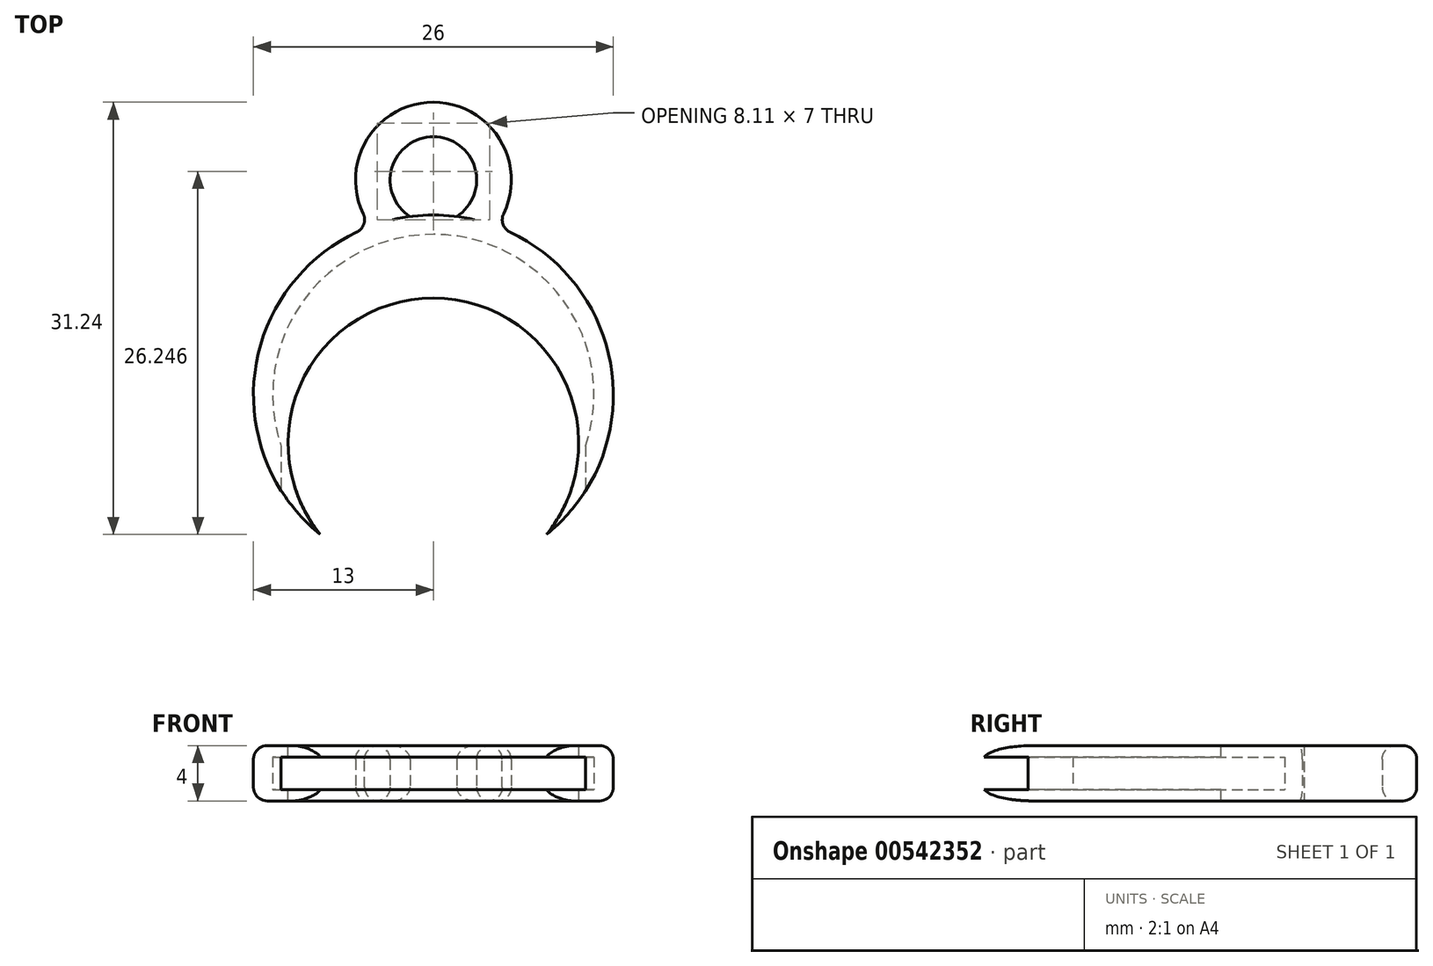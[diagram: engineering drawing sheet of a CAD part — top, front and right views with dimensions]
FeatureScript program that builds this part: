
annotation { "Feature Type Name" : "Feature", "Feature Type Description" : "" }
export const myFeature = defineFeature(function(context is Context, id is Id, definition is map)
    precondition{}
    {
        {
            var Q0;
            Q0=qCreatedBy(makeId("Top.planeOp"),FACE);
            var sketch = newSketch(context, id + "F0", { "sketchPlane" : qUnion([Q0])});
            skCircle(sketch, "E0", {"center": v(0, 0) * mm, "radius": 13 * mm});
            skArc(sketch, "E1", {"start": v(4.53, 12.19) * mm, "mid": v(0, 21.15) * mm, "end": v(-4.53, 12.19) * mm});
            skArc(sketch, "E2", {"start": v(1.68, 12.9) * mm, "mid": v(0, 18.65) * mm, "end": v(-1.68, 12.9) * mm});
            skSolve(sketch);
        }
        {
            var Q0;
            {var subQ0=sQuery(id+"F0.wireOp",EDGE,"E1");var subQ1=sQuery(id+"F0.wireOp",EDGE,"E0");var subQ2=makeQuery(id+"F0.imprint","INTERSECT",VERTEX,{"disambiguationData":[OD(0.0)],"derivedFrom":[subQ1,subQ0]});Q0=makeQuery(id+"F0.imprint","IMPRINT",FACE,{"disambiguationData":[TD([[makeQuery(id+"F0.imprint","IMPRINT",EDGE,{"disambiguationData":[TD([[subQ2,-1.0]])],"derivedFrom":subQ1}),1.0]])]});}
            var Q1;
            {var subQ0=sQuery(id+"F0.wireOp",EDGE,"E1");Q1=makeQuery(id+"F0.imprint","IMPRINT",FACE,{"disambiguationData":[TD([[makeQuery(id+"F0.imprint","IMPRINT",EDGE,{"derivedFrom":subQ0}),1.0]])]});}
            extrude(context, id + "F1", {"entities" : qUnion([Q0, Q1]), "endBound" : BoundingType.SYMMETRIC, "depth" : 4 * mm, "offsetDistance" : 25 * mm});
        }
        {
            var Q0;
            {var subQ0=sQuery(id+"F0.wireOp",EDGE,"E1");var subQ1=sQuery(id+"F0.wireOp",EDGE,"E0");Q0=makeQuery(id+"F1.opExtrude","SWEPT_EDGE",EDGE,{"disambiguationData":[OSD([subQ1,subQ0]),TDD([makeQuery(id+"F0.imprint","INTERSECT",VERTEX,{"disambiguationData":[OD(0.0)],"derivedFrom":[subQ1,subQ0]})])]});}
            fillet(context, id + "F2", {"entities" : qUnion([Q0]), "radius" : 1 * mm, "tangentPropagation" : true, "allowEdgeOverflow" : false});
        }
        {
            var Q0;
            {var subQ0=sQuery(id+"F0.wireOp",EDGE,"E1");var subQ1=sQuery(id+"F0.wireOp",EDGE,"E0");Q0=makeQuery(id+"F1.opExtrude","SWEPT_EDGE",EDGE,{"disambiguationData":[OSD([subQ1,subQ0]),TDD([makeQuery(id+"F0.imprint","INTERSECT",VERTEX,{"disambiguationData":[OD(1.0)],"derivedFrom":[subQ1,subQ0]})])]});}
            fillet(context, id + "F3", {"entities" : qUnion([Q0]), "radius" : 1 * mm, "tangentPropagation" : true, "allowEdgeOverflow" : false});
        }
        {
            var Q0;
            Q0=makeQuery(id+"F1.opExtrude","CAP_EDGE",EDGE,{"disambiguationData":[OSD([sQuery(id+"F0.wireOp",EDGE,"E2")])],"isStart":false});
            fillet(context, id + "F4", {"entities" : qUnion([Q0]), "radius" : 1 * mm, "tangentPropagation" : true, "allowEdgeOverflow" : false});
        }
        {
            var Q0;
            Q0=makeQuery(id+"F1.opExtrude","CAP_EDGE",EDGE,{"disambiguationData":[OSD([sQuery(id+"F0.wireOp",EDGE,"E2")])],"isStart":true});
            fillet(context, id + "F5", {"entities" : qUnion([Q0]), "radius" : 1 * mm, "tangentPropagation" : true, "allowEdgeOverflow" : false});
        }
        {
            var Q0;
            Q0=qCreatedBy(makeId("Top.planeOp"),FACE);
            var sketch = newSketch(context, id + "F6", { "sketchPlane" : qUnion([Q0])});
            skCircle(sketch, "E3", {"center": v(0, -3.5) * mm, "radius": 10.5 * mm});
            skSolve(sketch);
        }
        {
            var Q0;
            Q0 = qSketchRegion(id + "F6", true);
            extrude(context, id + "F7", {"entities" : qUnion([Q0]), "operationType" : NewBodyOperationType.REMOVE, "endBound" : BoundingType.SYMMETRIC, "oppositeDirection" : true, "depth" : 25 * mm, "offsetDistance" : 25 * mm});
        }
        {
            var Q0;
            Q0=qCreatedBy(makeId("Top.planeOp"),FACE);
            var sketch = newSketch(context, id + "F8", { "sketchPlane" : qUnion([Q0])});
            skCircle(sketch, "E4", {"center": v(0, 0) * mm, "radius": 11.6 * mm});
            skLineSegment(sketch, "E5.bottom", {"start": v(-11, -3.7) * mm, "end": v(11, -3.7) * mm});
            skLineSegment(sketch, "E5.top", {"start": v(-11, -18.04) * mm, "end": v(11, -18.04) * mm});
            skLineSegment(sketch, "E5.left", {"start": v(-11, -3.7) * mm, "end": v(-11, -18.04) * mm});
            skLineSegment(sketch, "E5.right", {"start": v(11, -3.7) * mm, "end": v(11, -18.04) * mm});
            skSolve(sketch);
        }
        {
            var Q0;
            Q0 = qSketchRegion(id + "F8", true);
            extrude(context, id + "F9", {"entities" : qUnion([Q0]), "operationType" : NewBodyOperationType.REMOVE, "endBound" : BoundingType.SYMMETRIC, "depth" : 2.34 * mm, "offsetDistance" : 25 * mm});
        }
        {
            var Q0;
            {var subQ0=sQuery(id+"F0.wireOp",EDGE,"E1");var subQ1=sQuery(id+"F0.wireOp",EDGE,"E0");var subQ2=makeQuery(id+"F0.imprint","IMPRINT",EDGE,{"disambiguationData":[TD([[makeQuery(id+"F0.imprint","INTERSECT",VERTEX,{"disambiguationData":[OD(0.0)],"derivedFrom":[subQ1,subQ0]}),1.0]])],"derivedFrom":subQ1});Q0=makeQuery(id+"F7.boolean.opBoolean","SPLIT",EDGE,{"disambiguationData":[TD([makeQuery(id+"F2.opFillet","BLEND_FACE",FACE,{"disambiguationData":[OSD([subQ1,subQ0])]})])],"derivedFrom":makeQuery(id+"F1.opExtrude","CAP_EDGE",EDGE,{"disambiguationData":[OSD([subQ1]),TDD([subQ2])],"isStart":false})});}
            var Q1;
            {var subQ0=sQuery(id+"F0.wireOp",EDGE,"E1");var subQ1=sQuery(id+"F0.wireOp",EDGE,"E0");var subQ2=makeQuery(id+"F0.imprint","IMPRINT",EDGE,{"disambiguationData":[TD([[makeQuery(id+"F0.imprint","INTERSECT",VERTEX,{"disambiguationData":[OD(0.0)],"derivedFrom":[subQ1,subQ0]}),1.0]])],"derivedFrom":subQ1});Q1=makeQuery(id+"F7.boolean.opBoolean","SPLIT",EDGE,{"disambiguationData":[TD([makeQuery(id+"F3.opFillet","BLEND_FACE",FACE,{"disambiguationData":[OSD([subQ1,subQ0])]})])],"derivedFrom":makeQuery(id+"F1.opExtrude","CAP_EDGE",EDGE,{"disambiguationData":[OSD([subQ1]),TDD([subQ2])],"isStart":false})});}
            var Q2;
            Q2=makeQuery(id+"F1.opExtrude","CAP_EDGE",EDGE,{"disambiguationData":[OSD([sQuery(id+"F0.wireOp",EDGE,"E1")])],"isStart":false});
            var Q3;
            Q3=makeQuery(id+"F1.opExtrude","CAP_EDGE",EDGE,{"disambiguationData":[OSD([sQuery(id+"F0.wireOp",EDGE,"E1")])],"isStart":true});
            var Q4;
            {var subQ0=sQuery(id+"F0.wireOp",EDGE,"E1");var subQ1=sQuery(id+"F0.wireOp",EDGE,"E0");Q4=makeQuery(id+"F3.opFillet","BLEND_EDGE",EDGE,{"blendedFrom":[makeQuery(id+"F1.opExtrude","SWEPT_EDGE",EDGE,{"disambiguationData":[OSD([subQ1,subQ0]),TDD([makeQuery(id+"F0.imprint","INTERSECT",VERTEX,{"disambiguationData":[OD(1.0)],"derivedFrom":[subQ1,subQ0]})])]}),makeQuery(id+"F1.opExtrude","CAP_FACE",FACE,{"disambiguationData":[OSD([subQ1,subQ0,sQuery(id+"F0.wireOp",EDGE,"E2")])],"isStart":true})],"blendedInto":[makeQuery(id+"F1.opExtrude","CAP_FACE",FACE,{"disambiguationData":[OSD([subQ1,subQ0,sQuery(id+"F0.wireOp",EDGE,"E2")])],"isStart":true})]});}
            var Q5;
            {var subQ0=sQuery(id+"F0.wireOp",EDGE,"E1");var subQ1=sQuery(id+"F0.wireOp",EDGE,"E0");Q5=makeQuery(id+"F3.opFillet","BLEND_EDGE",EDGE,{"blendedFrom":[makeQuery(id+"F1.opExtrude","SWEPT_EDGE",EDGE,{"disambiguationData":[OSD([subQ1,subQ0]),TDD([makeQuery(id+"F0.imprint","INTERSECT",VERTEX,{"disambiguationData":[OD(1.0)],"derivedFrom":[subQ1,subQ0]})])]}),makeQuery(id+"F1.opExtrude","CAP_FACE",FACE,{"disambiguationData":[OSD([subQ1,subQ0,sQuery(id+"F0.wireOp",EDGE,"E2")])],"isStart":false})],"blendedInto":[makeQuery(id+"F1.opExtrude","CAP_FACE",FACE,{"disambiguationData":[OSD([subQ1,subQ0,sQuery(id+"F0.wireOp",EDGE,"E2")])],"isStart":false})]});}
            var Q6;
            {var subQ0=sQuery(id+"F0.wireOp",EDGE,"E1");var subQ1=sQuery(id+"F0.wireOp",EDGE,"E0");var subQ2=makeQuery(id+"F0.imprint","IMPRINT",EDGE,{"disambiguationData":[TD([[makeQuery(id+"F0.imprint","INTERSECT",VERTEX,{"disambiguationData":[OD(0.0)],"derivedFrom":[subQ1,subQ0]}),1.0]])],"derivedFrom":subQ1});Q6=makeQuery(id+"F7.boolean.opBoolean","SPLIT",EDGE,{"disambiguationData":[TD([makeQuery(id+"F3.opFillet","BLEND_FACE",FACE,{"disambiguationData":[OSD([subQ1,subQ0])]})])],"derivedFrom":makeQuery(id+"F1.opExtrude","CAP_EDGE",EDGE,{"disambiguationData":[OSD([subQ1]),TDD([subQ2])],"isStart":true})});}
            var Q7;
            {var subQ0=sQuery(id+"F0.wireOp",EDGE,"E1");var subQ1=sQuery(id+"F0.wireOp",EDGE,"E0");Q7=makeQuery(id+"F2.opFillet","BLEND_EDGE",EDGE,{"blendedFrom":[makeQuery(id+"F1.opExtrude","SWEPT_EDGE",EDGE,{"disambiguationData":[OSD([subQ1,subQ0]),TDD([makeQuery(id+"F0.imprint","INTERSECT",VERTEX,{"disambiguationData":[OD(0.0)],"derivedFrom":[subQ1,subQ0]})])]}),makeQuery(id+"F1.opExtrude","CAP_FACE",FACE,{"disambiguationData":[OSD([subQ1,subQ0,sQuery(id+"F0.wireOp",EDGE,"E2")])],"isStart":true})],"blendedInto":[makeQuery(id+"F1.opExtrude","CAP_FACE",FACE,{"disambiguationData":[OSD([subQ1,subQ0,sQuery(id+"F0.wireOp",EDGE,"E2")])],"isStart":true})]});}
            var Q8;
            {var subQ0=sQuery(id+"F0.wireOp",EDGE,"E1");var subQ1=sQuery(id+"F0.wireOp",EDGE,"E0");Q8=makeQuery(id+"F2.opFillet","BLEND_EDGE",EDGE,{"blendedFrom":[makeQuery(id+"F1.opExtrude","SWEPT_EDGE",EDGE,{"disambiguationData":[OSD([subQ1,subQ0]),TDD([makeQuery(id+"F0.imprint","INTERSECT",VERTEX,{"disambiguationData":[OD(0.0)],"derivedFrom":[subQ1,subQ0]})])]}),makeQuery(id+"F1.opExtrude","CAP_FACE",FACE,{"disambiguationData":[OSD([subQ1,subQ0,sQuery(id+"F0.wireOp",EDGE,"E2")])],"isStart":false})],"blendedInto":[makeQuery(id+"F1.opExtrude","CAP_FACE",FACE,{"disambiguationData":[OSD([subQ1,subQ0,sQuery(id+"F0.wireOp",EDGE,"E2")])],"isStart":false})]});}
            fillet(context, id + "F10", {"entities" : qUnion([Q0, Q1, Q2, Q3, Q4, Q5, Q6, Q7, Q8]), "radius" : 1 * mm, "tangentPropagation" : true, "allowEdgeOverflow" : false});
        }
    });
